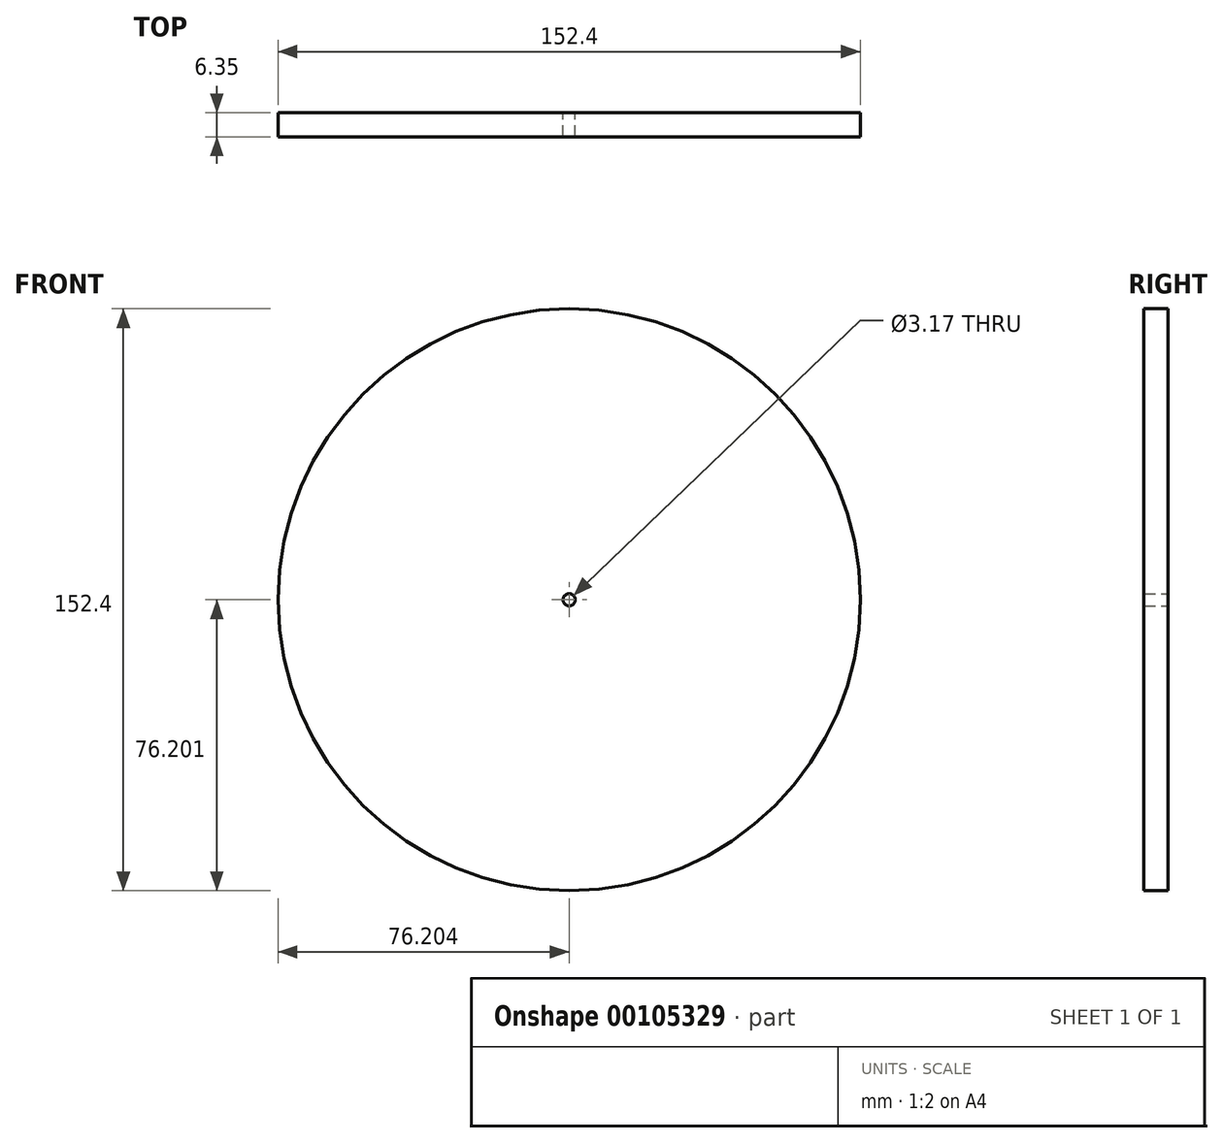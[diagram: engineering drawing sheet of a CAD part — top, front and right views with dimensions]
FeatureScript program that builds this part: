
annotation { "Feature Type Name" : "Feature", "Feature Type Description" : "" }
export const myFeature = defineFeature(function(context is Context, id is Id, definition is map)
    precondition{}
    {
        {
            var Q0;
            Q0=qCreatedBy(makeId("Front.planeOp"),FACE);
            var sketch = newSketch(context, id + "F0", { "sketchPlane" : qUnion([Q0])});
            skCircle(sketch, "E0", {"center": v(-51.23, 54.64) * mm, "radius": 76.2 * mm});
            skCircle(sketch, "E1", {"center": v(-51.23, 54.64) * mm, "radius": 1.59 * mm});
            skSolve(sketch);
        }
        {
            var Q0;
            Q0=makeQuery(id+"F0.imprint","IMPRINT",FACE,{"disambiguationData":[TD([[makeQuery(id+"F0.imprint","IMPRINT",EDGE,{"derivedFrom":sQuery(id+"F0.wireOp",EDGE,"E0")}),1.0]])]});
            extrude(context, id + "F1", {"entities" : qUnion([Q0]), "depth" : 6.35 * mm});
        }
    });
